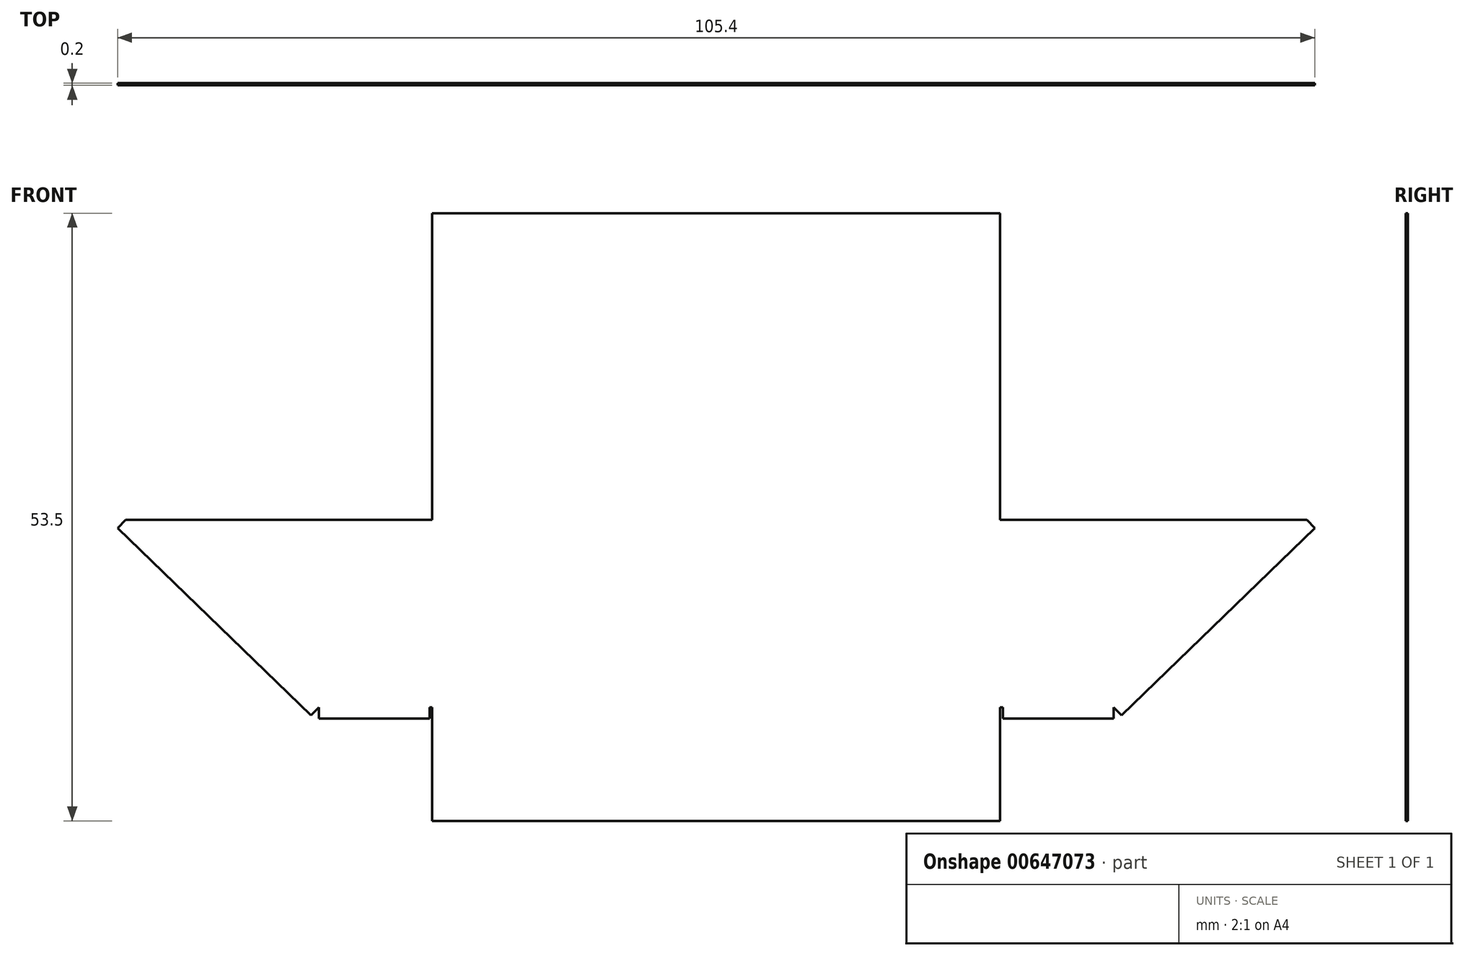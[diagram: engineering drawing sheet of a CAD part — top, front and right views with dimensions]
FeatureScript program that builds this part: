
annotation { "Feature Type Name" : "Feature", "Feature Type Description" : "" }
export const myFeature = defineFeature(function(context is Context, id is Id, definition is map)
    precondition{}
    {
        {
            var Q0;
            Q0=qCreatedBy(makeId("Front.planeOp"),FACE);
            var sketch = newSketch(context, id + "F0", { "sketchPlane" : qUnion([Q0])});
            skLineSegment(sketch, "E0.bottom", {"start": v(-25, 8.25) * mm, "end": v(25, 8.25) * mm});
            skLineSegment(sketch, "E0.top", {"start": v(-25, -8.25) * mm, "end": v(25, -8.25) * mm});
            skLineSegment(sketch, "E0.left", {"start": v(-25, 8.25) * mm, "end": v(-25, -8.25) * mm});
            skLineSegment(sketch, "E0.right", {"start": v(25, 8.25) * mm, "end": v(25, -8.25) * mm});
            skPoint(sketch, "E0.middle", {"position": v(0, 0) * mm});
            skLineSegment(sketch, "E1", {"start": v(-25, 8.25) * mm, "end": v(-52, 8.25) * mm});
            skLineSegment(sketch, "E2", {"start": v(-52, 8.25) * mm, "end": v(-35, -8.25) * mm});
            skLineSegment(sketch, "E3", {"start": v(-35, -8.25) * mm, "end": v(-25, -8.25) * mm});
            skLineSegment(sketch, "E4", {"start": v(35, -8.25) * mm, "end": v(25, -8.25) * mm});
            skLineSegment(sketch, "E5", {"start": v(25, 8.25) * mm, "end": v(25, 35.25) * mm});
            skLineSegment(sketch, "E6", {"start": v(25, 35.25) * mm, "end": v(-25, 35.25) * mm});
            skLineSegment(sketch, "E7", {"start": v(-25, 35.25) * mm, "end": v(-25, 8.25) * mm});
            skLineSegment(sketch, "E8", {"start": v(-25, -8.25) * mm, "end": v(-25, -18.25) * mm});
            skLineSegment(sketch, "E9", {"start": v(-25, -18.25) * mm, "end": v(25, -18.25) * mm});
            skLineSegment(sketch, "E10", {"start": v(25, -18.25) * mm, "end": v(25, -8.25) * mm});
            skLineSegment(sketch, "E11", {"start": v(25, 8.25) * mm, "end": v(52, 8.25) * mm});
            skLineSegment(sketch, "E12", {"start": v(52, 8.25) * mm, "end": v(35, -8.25) * mm});
            skLineSegment(sketch, "E13", {"start": v(52, 8.25) * mm, "end": v(52.7, 7.53) * mm});
            skLineSegment(sketch, "E14", {"start": v(35, -8.25) * mm, "end": v(35.7, -8.97) * mm});
            skLineSegment(sketch, "E15", {"start": v(52.7, 7.53) * mm, "end": v(35.7, -8.97) * mm});
            skLineSegment(sketch, "E16", {"start": v(-52, 8.25) * mm, "end": v(-52.7, 7.53) * mm});
            skLineSegment(sketch, "E17", {"start": v(-35, -8.25) * mm, "end": v(-35.7, -8.97) * mm});
            skLineSegment(sketch, "E18", {"start": v(-35.7, -8.97) * mm, "end": v(-52.7, 7.53) * mm});
            skLineSegment(sketch, "E19.0", {"start": v(35, -9.25) * mm, "end": v(25.25, -9.25) * mm});
            skLineSegment(sketch, "E20.0", {"start": v(-35, -9.25) * mm, "end": v(-25.25, -9.25) * mm});
            skLineSegment(sketch, "E21", {"start": v(-35, -9.25) * mm, "end": v(-35, -8.25) * mm});
            skLineSegment(sketch, "E22", {"start": v(35, -9.25) * mm, "end": v(35, -8.25) * mm});
            skLineSegment(sketch, "E23.0", {"start": v(25.25, -9.25) * mm, "end": v(25.25, -8.25) * mm});
            skLineSegment(sketch, "E24.0", {"start": v(-25.25, -8.25) * mm, "end": v(-25.25, -9.25) * mm});
            skSolve(sketch);
        }
        {
            var Q0;
            Q0 = qSketchRegion(id + "F0", true);
            extrude(context, id + "F1", {"entities" : qUnion([Q0]), "depth" : .2 * mm, "offsetDistance" : 25 * mm});
        }
    });
